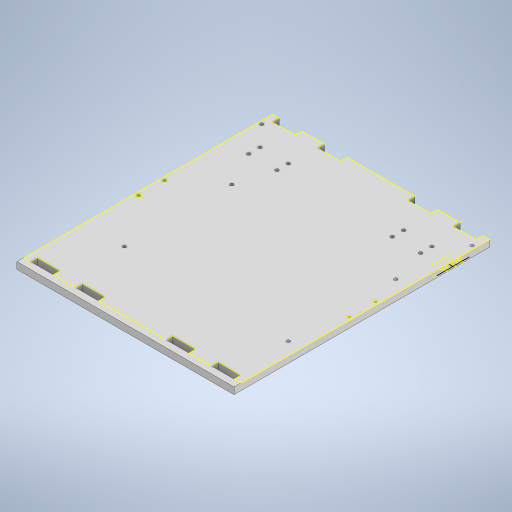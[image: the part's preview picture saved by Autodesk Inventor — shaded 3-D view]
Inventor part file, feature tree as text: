
AUTODESK INVENTOR PART (.ipt)
format: ipt  version: 2024.2 (Build 282272000, 272)  size: 431,104 bytes
history: native  units: mm
features: reference x103, other x9, sketch x8, extrude x7, mirror x2, projected_geometry x1
ambient origin geometry x8: Origin, YZ Plane, XZ Plane, XY Plane, X Axis, Y Axis, Z Axis, Center Point
bodies: Body1 (feature_tree)
feature tree (130):
  extrude  "Выдавливание2"  Depth=192.0mm
  extrude  "Выдавливание3"  Depth=170.0mm
  other  "РабПлоскость1"
  mirror  "Зеркальное отражение1"
  extrude  "Выдавливание4"  Depth=220.0mm
  sketch  "Эскиз4"
  extrude  "Выдавливание5"  Depth=11.0mm
  other  "РабПлоскость2"
  mirror  "Зеркальное отражение2"
  extrude  "Выдавливание6"  Depth=3.0mm
  extrude  "Выдавливание7"  Depth=3.0mm
  extrude  "Выдавливание8"  Depth=3.0mm
  sketch  "Эскиз1"
  sketch  "Эскиз2"
  sketch  "Эскиз3"
  reference  "Ссылка1"
  reference  "Ссылка2"
  reference  "Ссылка3"
  reference  "Ссылка4"
  projected_geometry  "Спроецированная петля1"
  reference  "Ссылка5"
  reference  "Ссылка6"
  reference  "Ссылка7"
  reference  "Ссылка8"
  reference  "Ссылка9"
  reference  "Ссылка10"
  reference  "Ссылка11"
  reference  "Ссылка12"
  reference  "Ссылка13"
  reference  "Ссылка14"
  reference  "Ссылка15"
  reference  "Ссылка16"
  reference  "Ссылка17"
  reference  "Ссылка18"
  reference  "Ссылка19"
  reference  "Ссылка20"
  reference  "Ссылка21"
  reference  "Ссылка22"
  reference  "Ссылка23"
  reference  "Ссылка24"
  reference  "Ссылка25"
  reference  "Ссылка26"
  reference  "Ссылка27"
  reference  "Ссылка28"
  reference  "Ссылка29"
  reference  "Ссылка30"
  reference  "Ссылка31"
  reference  "Ссылка32"
  reference  "Ссылка33"
  reference  "Ссылка34"
  reference  "Ссылка35"
  reference  "Ссылка36"
  reference  "Ссылка37"
  reference  "Ссылка38"
  reference  "Ссылка39"
  reference  "Ссылка40"
  reference  "Ссылка41"
  reference  "Ссылка42"
  reference  "Ссылка43"
  reference  "Ссылка44"
  reference  "Ссылка45"
  reference  "Ссылка46"
  reference  "Ссылка47"
  reference  "Ссылка48"
  reference  "Ссылка49"
  reference  "Ссылка50"
  reference  "Ссылка51"
  reference  "Ссылка52"
  reference  "Ссылка53"
  reference  "Ссылка54"
  reference  "Ссылка55"
  reference  "Ссылка56"
  reference  "Ссылка57"
  reference  "Ссылка58"
  reference  "Ссылка59"
  reference  "Ссылка60"
  reference  "Ссылка61"
  reference  "Ссылка62"
  reference  "Ссылка63"
  reference  "Ссылка64"
  reference  "Ссылка65"
  reference  "Ссылка66"
  reference  "Ссылка67"
  reference  "Ссылка68"
  reference  "Ссылка69"
  reference  "Ссылка70"
  reference  "Ссылка71"
  reference  "Ссылка72"
  reference  "Ссылка73"
  reference  "Ссылка74"
  reference  "Ссылка75"
  reference  "Ссылка76"
  reference  "Ссылка77"
  reference  "Ссылка78"
  reference  "Ссылка79"
  reference  "Ссылка80"
  reference  "Ссылка81"
  reference  "Ссылка82"
  reference  "Ссылка83"
  reference  "Ссылка84"
  reference  "Ссылка85"
  reference  "Ссылка86"
  reference  "Ссылка87"
  reference  "Ссылка88"
  reference  "Ссылка89"
  reference  "Ссылка90"
  reference  "Ссылка91"
  reference  "Ссылка92"
  reference  "Ссылка93"
  reference  "Ссылка94"
  reference  "Ссылка95"
  reference  "Ссылка96"
  reference  "Ссылка97"
  reference  "Ссылка98"
  reference  "Ссылка99"
  reference  "Ссылка100"
  reference  "Ссылка101"
  reference  "Ссылка102"
  reference  "Ссылка103"
  sketch  "Эскиз5"
  sketch  "Эскиз6"
  sketch  "Эскиз7"
  sketch  "Эскиз8"
  other  "<userpath>\Documents\Artist\3D\Робот.iam"
  other  "Робот.iam"
  other  "крепление подшипника_1:1"
  other  "боковая стенка:1"
  other  "Проецирование ребер1"
  other  "Проецирование ребер2"
  other  "Проецирование ребер3"
